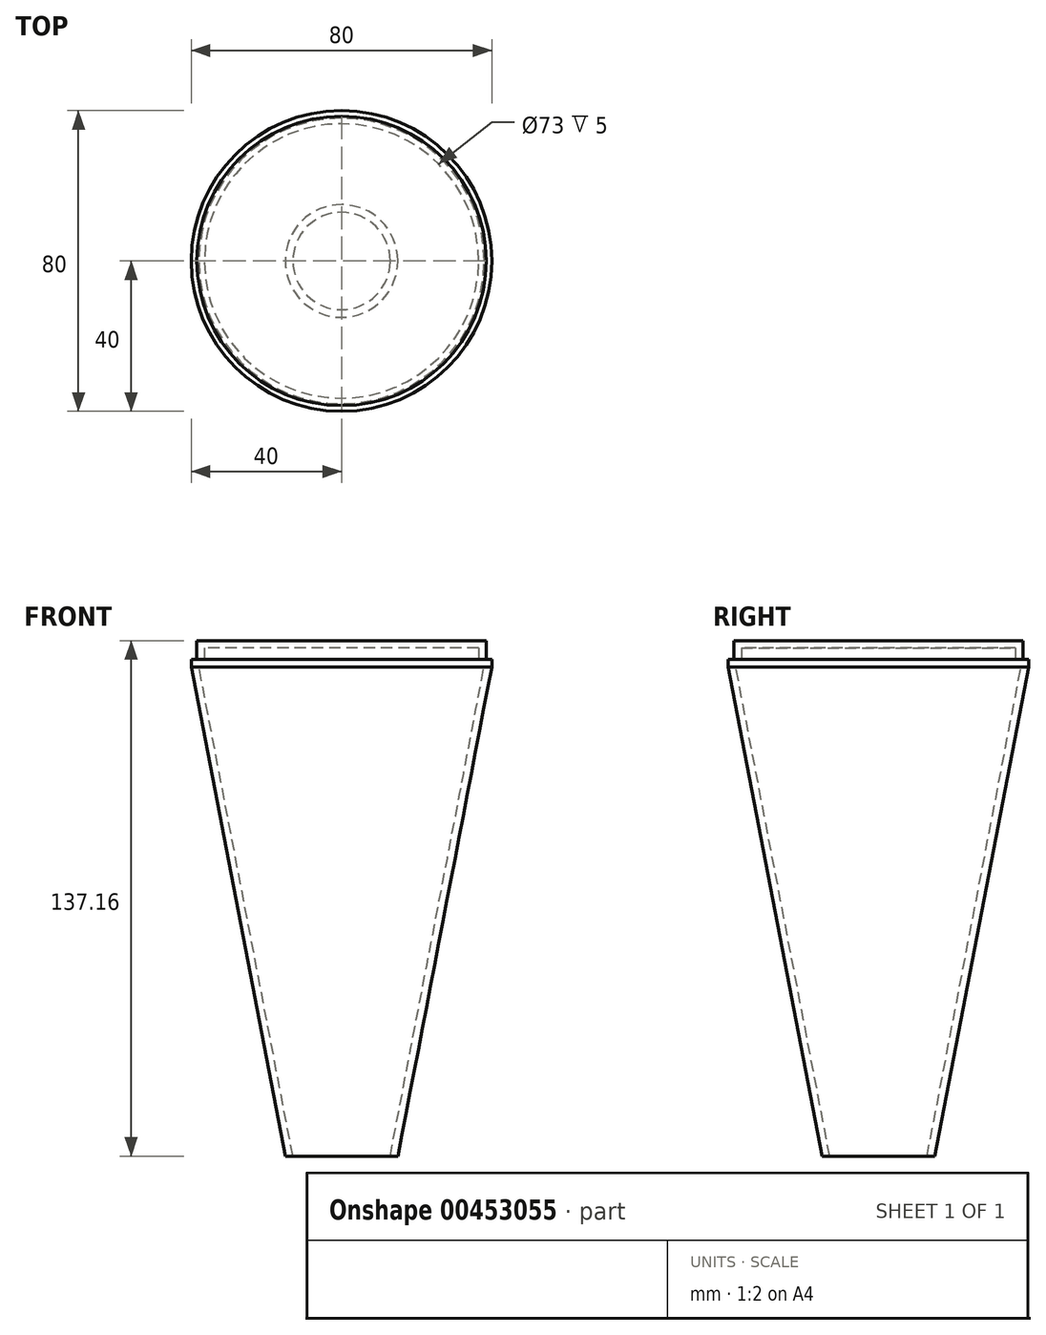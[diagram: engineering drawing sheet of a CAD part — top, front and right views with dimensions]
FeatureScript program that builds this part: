
annotation { "Feature Type Name" : "Feature", "Feature Type Description" : "" }
export const myFeature = defineFeature(function(context is Context, id is Id, definition is map)
    precondition{}
    {
        {
            var Q0;
            Q0=qCreatedBy(makeId("Top.planeOp"),FACE);
            var sketch = newSketch(context, id + "F0", { "sketchPlane" : qUnion([Q0])});
            skCircle(sketch, "E0", {"center": v(0, 0) * mm, "radius": 40 * mm});
            skSolve(sketch);
        }
        {
            var Q0;
            Q0=makeQuery(id+"F0.imprint","IMPRINT",FACE,{"disambiguationData":[TD([[makeQuery(id+"F0.imprint","IMPRINT",EDGE,{"derivedFrom":sQuery(id+"F0.wireOp",EDGE,"E0")}),1.0]])]});
            extrude(context, id + "F1", {"entities" : qUnion([Q0]), "depth" : 2 * mm});
        }
        {
            var Q0;
            Q0=makeQuery(id+"F1.opExtrude","CAP_FACE",FACE,{"disambiguationData":[OSD([sQuery(id+"F0.wireOp",EDGE,"E0")])],"isStart":false});
            var sketch = newSketch(context, id + "F2", { "sketchPlane" : qUnion([Q0])});
            skCircle(sketch, "E1", {"center": v(0, 0) * mm, "radius": 38.5 * mm});
            skSolve(sketch);
        }
        {
            var Q0;
            Q0=makeQuery(id+"F2.imprint","IMPRINT",FACE,{"disambiguationData":[TD([[makeQuery(id+"F2.imprint","IMPRINT",EDGE,{"derivedFrom":sQuery(id+"F2.wireOp",EDGE,"E1")}),1.0]])]});
            extrude(context, id + "F3", {"entities" : qUnion([Q0]), "operationType" : NewBodyOperationType.ADD, "depth" : 5 * mm});
        }
        {
            var Q0;
            Q0=makeQuery(id+"F1.opExtrude","CAP_FACE",FACE,{"disambiguationData":[OSD([sQuery(id+"F0.wireOp",EDGE,"E0")])],"isStart":true});
            var sketch = newSketch(context, id + "F4", { "sketchPlane" : qUnion([Q0])});
            skSolve(sketch);
        }
        {
            var Q0;
            Q0=qCreatedBy(makeId("Right.planeOp"),FACE);
            var sketch = newSketch(context, id + "F5", { "sketchPlane" : qUnion([Q0])});
            skLineSegment(sketch, "E2", {"start": v(-7.78, -130.16) * mm, "end": v(7.77, -130.16) * mm});
            skSolve(sketch);
        }
        {
            var Q0;
            Q0=sQuery(id+"F5.wireOp",VERTEX,"E2.start");
            var Q1;
            Q1=qCreatedBy(makeId("Top.planeOp"),FACE);
            cPlane(context, id + "F6", {"entities" : qUnion([Q0, Q1]), "cplaneType" : CPlaneType.PLANE_POINT, "offset" : 25 * mm, "flipAlignment" : true, "width" : 150 * mm, "height" : 150 * mm});
        }
        {
            var Q0;
            Q0=qCreatedBy(id+"F6.planeOp",FACE);
            var sketch = newSketch(context, id + "F7", { "sketchPlane" : qUnion([Q0])});
            skCircle(sketch, "E3", {"center": v(0, 0) * mm, "radius": 15 * mm});
            skSolve(sketch);
        }
        {
            var Q1;
            Q1=makeQuery(id+"F7.imprint","IMPRINT",FACE,{"disambiguationData":[TD([[makeQuery(id+"F7.imprint","IMPRINT",EDGE,{"derivedFrom":sQuery(id+"F7.wireOp",EDGE,"E3")}),1.0]])]});
            var Q2;
            Q2=makeQuery(id+"F4.imprint","IMPRINT",FACE,{"disambiguationData":[TD([[makeQuery(id+"F4.imprint","IMPRINT",EDGE,{"derivedFrom":makeQuery(id+"F1.opExtrude","CAP_EDGE",EDGE,{"disambiguationData":[OSD([sQuery(id+"F0.wireOp",EDGE,"E0")])],"isStart":true})}),-1.0]])]});
            loft(context, id + "F8", {"operationType" : NewBodyOperationType.ADD, "sheetProfilesArray" : [{ "sheetProfileEntities" : qUnion([Q1]) }, { "sheetProfileEntities" : qUnion([Q2]) }]});
        }
        {
            var Q0;
            Q0=makeQuery(id+"F8.opLoft","CAP_FACE",FACE,{"disambiguationData":[OSD([makeQuery(id+"F7.imprint","IMPRINT",FACE,{"disambiguationData":[TD([[makeQuery(id+"F7.imprint","IMPRINT",EDGE,{"derivedFrom":sQuery(id+"F7.wireOp",EDGE,"E3")}),1.0]])]})])],"isStart":true});
            shell(context, id + "F9", {"entities" : qUnion([Q0]), "thickness" : 2 * mm});
        }
    });
